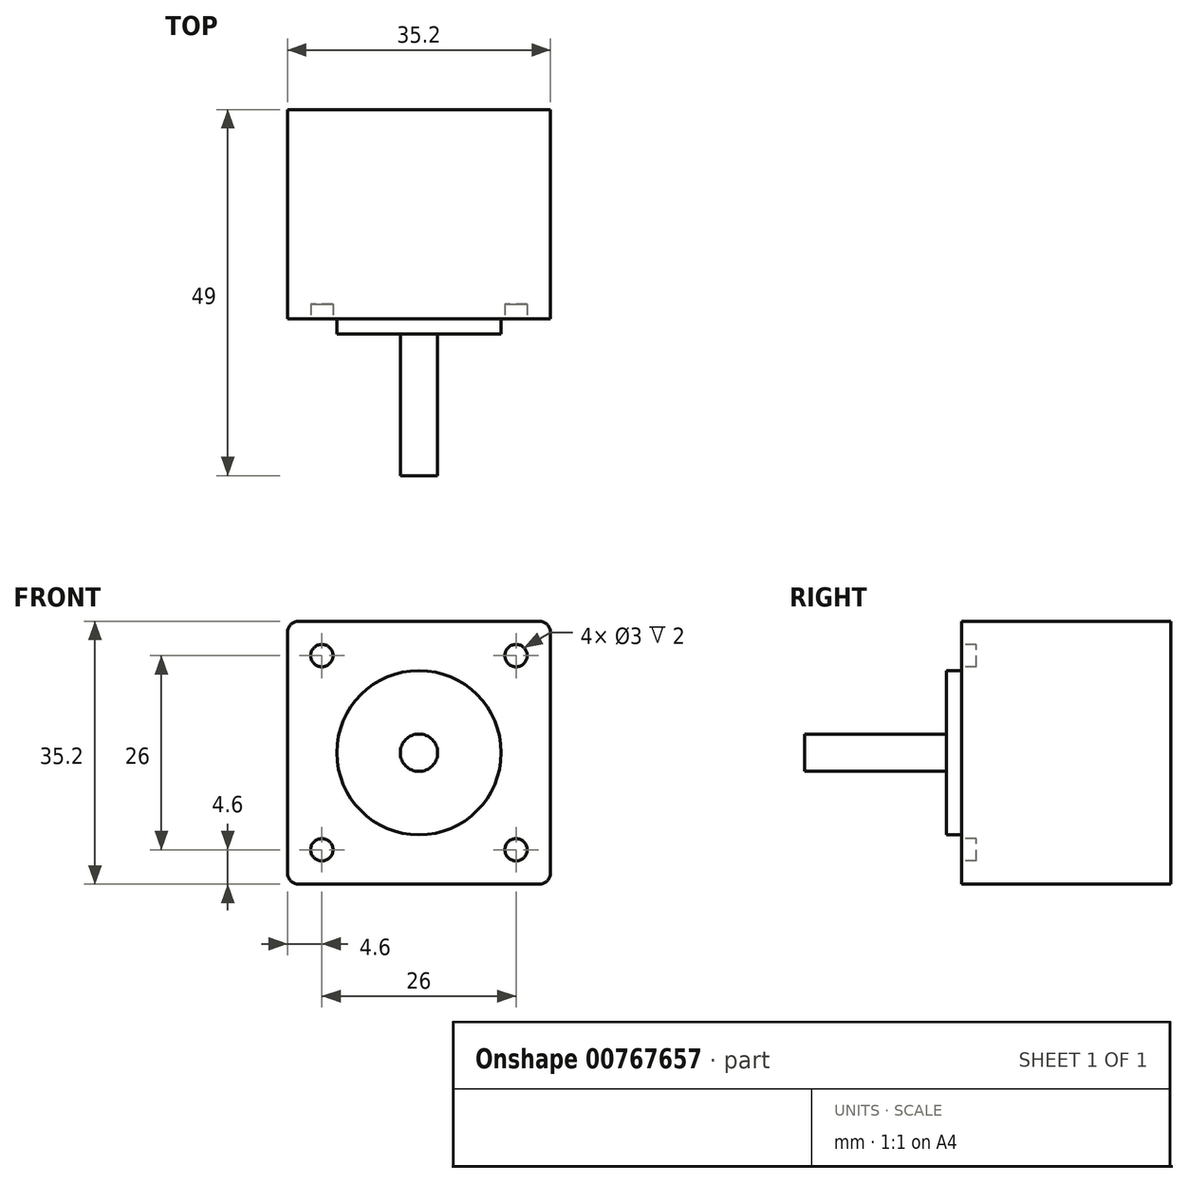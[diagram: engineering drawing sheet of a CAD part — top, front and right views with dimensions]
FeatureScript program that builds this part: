
annotation { "Feature Type Name" : "Feature", "Feature Type Description" : "" }
export const myFeature = defineFeature(function(context is Context, id is Id, definition is map)
    precondition{}
    {
        {
            var Q0;
            Q0=qCreatedBy(makeId("Front.planeOp"),FACE);
            var sketch = newSketch(context, id + "F0", { "sketchPlane" : qUnion([Q0])});
            skLineSegment(sketch, "E0.bottom", {"start": v(16.1, -17.6) * mm, "end": v(-16.1, -17.6) * mm});
            skLineSegment(sketch, "E0.top", {"start": v(16.1, 17.6) * mm, "end": v(-16.1, 17.6) * mm});
            skLineSegment(sketch, "E0.left", {"start": v(17.6, -16.1) * mm, "end": v(17.6, 16.1) * mm});
            skLineSegment(sketch, "E0.right", {"start": v(-17.6, -16.1) * mm, "end": v(-17.6, 16.1) * mm});
            skPoint(sketch, "E0.middle", {"position": v(0, 0) * mm});
            skPoint(sketch, "E1.visualSharp", {"position": v(-17.6, 17.6) * mm});
            skArc(sketch, "E1.filletArc", {"start": v(-16.1, 17.6) * mm, "mid": v(-17.16, 17.16) * mm, "end": v(-17.6, 16.1) * mm});
            skPoint(sketch, "E2.visualSharp", {"position": v(17.6, 17.6) * mm});
            skArc(sketch, "E2.filletArc", {"start": v(17.6, 16.1) * mm, "mid": v(17.16, 17.16) * mm, "end": v(16.1, 17.6) * mm});
            skPoint(sketch, "E3.visualSharp", {"position": v(17.6, -17.6) * mm});
            skArc(sketch, "E3.filletArc", {"start": v(16.1, -17.6) * mm, "mid": v(17.16, -17.16) * mm, "end": v(17.6, -16.1) * mm});
            skPoint(sketch, "E4.visualSharp", {"position": v(-17.6, -17.6) * mm});
            skArc(sketch, "E4.filletArc", {"start": v(-17.6, -16.1) * mm, "mid": v(-17.16, -17.16) * mm, "end": v(-16.1, -17.6) * mm});
            skSolve(sketch);
        }
        {
            var Q0;
            Q0 = qSketchRegion(id + "F0", true);
            extrude(context, id + "F1", {"entities" : qUnion([Q0]), "depth" : 28 * mm, "offsetDistance" : 25 * mm});
        }
        {
            var Q0;
            Q0=makeQuery(id+"F1.opExtrude","CAP_FACE",FACE,{"disambiguationData":[OSD([sQuery(id+"F0.wireOp",EDGE,"E0.bottom"),sQuery(id+"F0.wireOp",EDGE,"E0.top"),sQuery(id+"F0.wireOp",EDGE,"E0.left"),sQuery(id+"F0.wireOp",EDGE,"E0.right"),sQuery(id+"F0.wireOp",EDGE,"E1.filletArc"),sQuery(id+"F0.wireOp",EDGE,"E2.filletArc"),sQuery(id+"F0.wireOp",EDGE,"E3.filletArc"),sQuery(id+"F0.wireOp",EDGE,"E4.filletArc")])],"isStart":false});
            var sketch = newSketch(context, id + "F2", { "sketchPlane" : qUnion([Q0])});
            skCircle(sketch, "E5", {"center": v(0, 0) * mm, "radius": 11 * mm});
            skCircle(sketch, "E6", {"center": v(0, 0) * mm, "radius": 2.5 * mm});
            skLineSegment(sketch, "E7.bottom", {"start": v(13, -13) * mm, "end": v(-13, -13) * mm, "construction": true});
            skLineSegment(sketch, "E7.top", {"start": v(13, 13) * mm, "end": v(-13, 13) * mm, "construction": true});
            skLineSegment(sketch, "E7.left", {"start": v(13, -13) * mm, "end": v(13, 13) * mm, "construction": true});
            skLineSegment(sketch, "E7.right", {"start": v(-13, -13) * mm, "end": v(-13, 13) * mm, "construction": true});
            skCircle(sketch, "E8", {"center": v(-13, 13) * mm, "radius": 1.5 * mm});
            skCircle(sketch, "E9.1.0", {"center": v(-13, -13) * mm, "radius": 1.5 * mm});
            skCircle(sketch, "E9.2.0", {"center": v(13, -13) * mm, "radius": 1.5 * mm});
            skCircle(sketch, "E9.3.0", {"center": v(13, 13) * mm, "radius": 1.5 * mm});
            skSolve(sketch);
        }
        {
            var Q0;
            Q0=makeQuery(id+"F2.imprint","IMPRINT",FACE,{"disambiguationData":[TD([[makeQuery(id+"F2.imprint","IMPRINT",EDGE,{"derivedFrom":sQuery(id+"F2.wireOp",EDGE,"E5")}),1.0]])]});
            extrude(context, id + "F3", {"entities" : qUnion([Q0]), "operationType" : NewBodyOperationType.ADD, "depth" : 2 * mm, "offsetDistance" : 25 * mm});
        }
        {
            var Q0;
            Q0=makeQuery(id+"F2.imprint","IMPRINT",FACE,{"disambiguationData":[TD([[makeQuery(id+"F2.imprint","IMPRINT",EDGE,{"derivedFrom":sQuery(id+"F2.wireOp",EDGE,"E8")}),1.0]])]});
            var Q1;
            Q1=makeQuery(id+"F2.imprint","IMPRINT",FACE,{"disambiguationData":[TD([[makeQuery(id+"F2.imprint","IMPRINT",EDGE,{"derivedFrom":sQuery(id+"F2.wireOp",EDGE,"E9.3.0")}),1.0]])]});
            var Q2;
            Q2=makeQuery(id+"F2.imprint","IMPRINT",FACE,{"disambiguationData":[TD([[makeQuery(id+"F2.imprint","IMPRINT",EDGE,{"derivedFrom":sQuery(id+"F2.wireOp",EDGE,"E9.2.0")}),1.0]])]});
            var Q3;
            Q3=makeQuery(id+"F2.imprint","IMPRINT",FACE,{"disambiguationData":[TD([[makeQuery(id+"F2.imprint","IMPRINT",EDGE,{"derivedFrom":sQuery(id+"F2.wireOp",EDGE,"E9.1.0")}),1.0]])]});
            extrude(context, id + "F4", {"entities" : qUnion([Q0, Q1, Q2, Q3]), "operationType" : NewBodyOperationType.REMOVE, "oppositeDirection" : true, "depth" : 2 * mm, "offsetDistance" : 25 * mm});
        }
        {
            var Q0;
            Q0=makeQuery(id+"F2.imprint","IMPRINT",FACE,{"disambiguationData":[TD([[makeQuery(id+"F2.imprint","IMPRINT",EDGE,{"derivedFrom":sQuery(id+"F2.wireOp",EDGE,"E6")}),1.0]])]});
            extrude(context, id + "F5", {"entities" : qUnion([Q0]), "operationType" : NewBodyOperationType.ADD, "depth" : 21 * mm, "offsetDistance" : 25 * mm});
        }
    });
